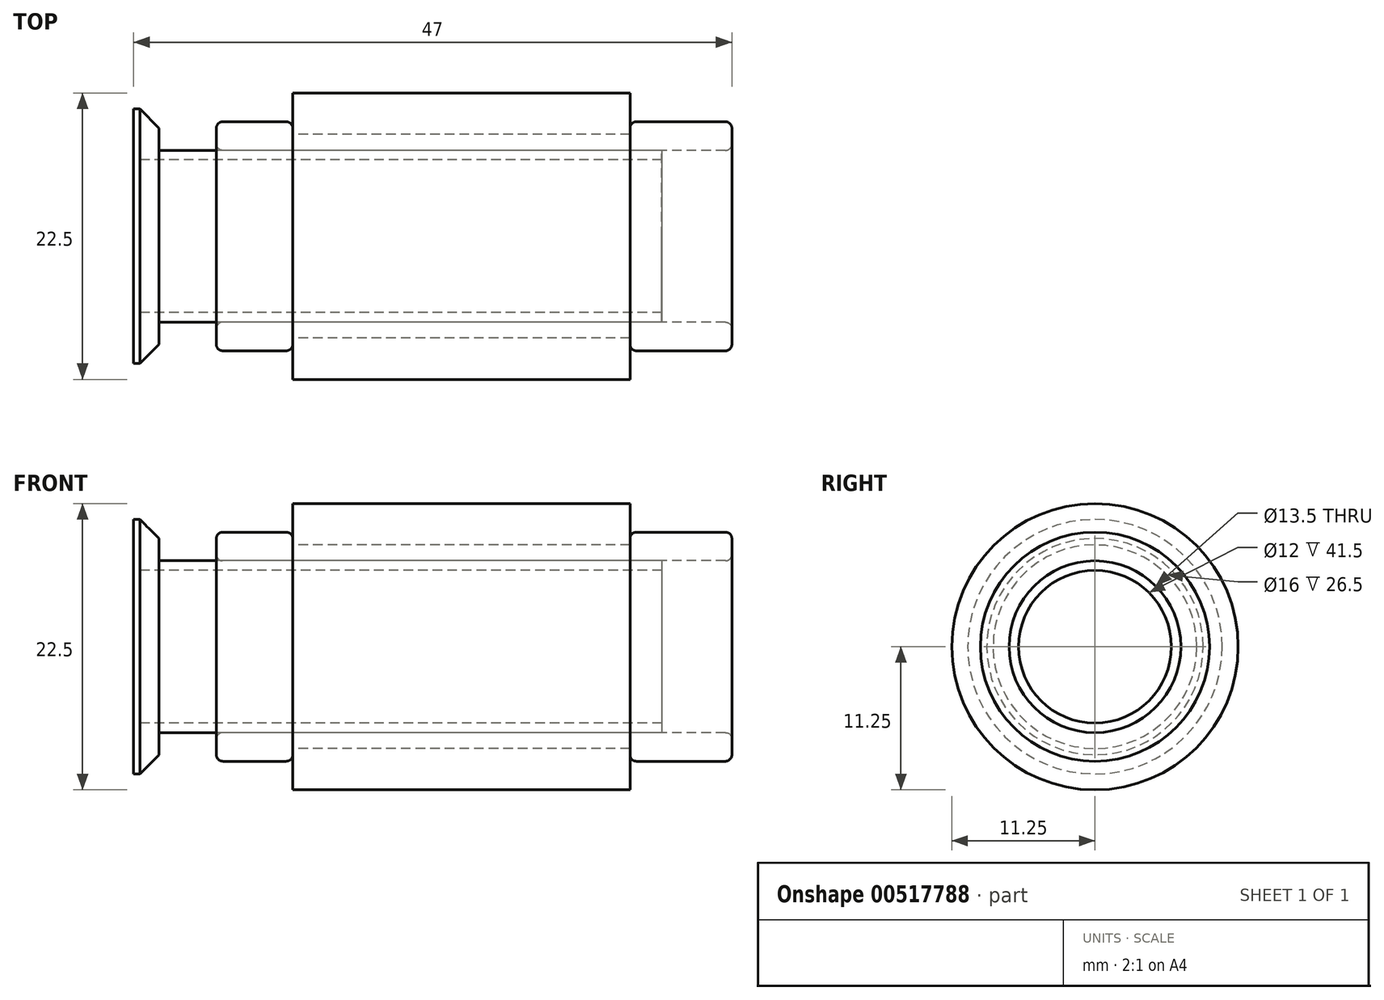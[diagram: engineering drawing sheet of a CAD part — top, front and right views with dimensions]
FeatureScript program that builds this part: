
annotation { "Feature Type Name" : "Feature", "Feature Type Description" : "" }
export const myFeature = defineFeature(function(context is Context, id is Id, definition is map)
    precondition{}
    {
        {
            var Q0;
            Q0=qCreatedBy(makeId("Front.planeOp"),FACE);
            var sketch = newSketch(context, id + "F0", { "sketchPlane" : qUnion([Q0])});
            skLineSegment(sketch, "E0.bottom", {"start": v(0, 11.25) * mm, "end": v(26.5, 11.25) * mm});
            skLineSegment(sketch, "E0.top", {"start": v(0, 8) * mm, "end": v(26.5, 8) * mm});
            skLineSegment(sketch, "E0.left", {"start": v(0, 11.25) * mm, "end": v(0, 8) * mm});
            skLineSegment(sketch, "E0.right", {"start": v(26.5, 11.25) * mm, "end": v(26.5, 8) * mm});
            skLineSegment(sketch, "E1", {"start": v(-6.13, 0) * mm, "end": v(35.82, 0) * mm});
            skSolve(sketch);
        }
        {
            var Q0;
            Q0 = qSketchRegion(id + "F0", true);
            var Q1;
            Q1=sQuery(id+"F0.wireOp",EDGE,"E1");
            revolve(context, id + "F1", {"entities" : qUnion([Q0]), "axis" : qUnion([Q1]), "revolveType" : RevolveType.FULL});
        }
        {
            var Q0;
            Q0=qCreatedBy(makeId("Front.planeOp"),FACE);
            var sketch = newSketch(context, id + "F2", { "sketchPlane" : qUnion([Q0])});
            skLineSegment(sketch, "E2", {"start": v(-10.5, 6.75) * mm, "end": v(29, 6.75) * mm});
            skLineSegment(sketch, "E3", {"start": v(29, 6.75) * mm, "end": v(29, 6) * mm});
            skLineSegment(sketch, "E4", {"start": v(29, 6) * mm, "end": v(-12.5, 6) * mm});
            skLineSegment(sketch, "E5", {"start": v(-12.5, 6) * mm, "end": v(-12.5, 10) * mm});
            skLineSegment(sketch, "E6", {"start": v(-12.5, 10) * mm, "end": v(-12, 10) * mm});
            skLineSegment(sketch, "E7", {"start": v(-12, 10) * mm, "end": v(-10.5, 8.5) * mm});
            skLineSegment(sketch, "E8", {"start": v(-10.5, 8.5) * mm, "end": v(-10.5, 6.75) * mm});
            skLineSegment(sketch, "E9", {"start": v(-7.68, 0) * mm, "end": v(-2.98, 0) * mm});
            skSolve(sketch);
        }
        {
            var Q0;
            Q0=makeQuery(id+"F2.imprint","IMPRINT",FACE,{"disambiguationData":[TD([[makeQuery(id+"F2.imprint","IMPRINT",EDGE,{"derivedFrom":sQuery(id+"F2.wireOp",EDGE,"E2")}),-1.0]])]});
            var Q1;
            Q1=sQuery(id+"F2.wireOp",EDGE,"E9");
            revolve(context, id + "F3", {"entities" : qUnion([Q0]), "axis" : qUnion([Q1]), "revolveType" : RevolveType.FULL});
        }
        {
            var Q0;
            Q0=qCreatedBy(makeId("Front.planeOp"),FACE);
            var sketch = newSketch(context, id + "F4", { "sketchPlane" : qUnion([Q0])});
            skLineSegment(sketch, "E10.bottom", {"start": v(-5.5, 9) * mm, "end": v(-0.5, 9) * mm});
            skLineSegment(sketch, "E10.left", {"start": v(-6, 8.5) * mm, "end": v(-6, 7.25) * mm});
            skLineSegment(sketch, "E10.right", {"start": v(0, 8.5) * mm, "end": v(0, 8) * mm});
            skLineSegment(sketch, "E11.bottom", {"start": v(27, 9) * mm, "end": v(34, 9) * mm});
            skLineSegment(sketch, "E11.top", {"start": v(26.5, 6.75) * mm, "end": v(34, 6.75) * mm});
            skLineSegment(sketch, "E11.left", {"start": v(26.5, 8.5) * mm, "end": v(26.5, 8) * mm});
            skLineSegment(sketch, "E11.right", {"start": v(34.5, 8.5) * mm, "end": v(34.5, 7.25) * mm});
            skLineSegment(sketch, "E12.bottom", {"start": v(0, 8) * mm, "end": v(26.5, 8) * mm});
            skLineSegment(sketch, "E12.top", {"start": v(-5.5, 6.75) * mm, "end": v(26.5, 6.75) * mm});
            skPoint(sketch, "E13.visualSharp", {"position": v(-6, 9) * mm});
            skArc(sketch, "E13.filletArc", {"start": v(-5.5, 9) * mm, "mid": v(-5.85, 8.85) * mm, "end": v(-6, 8.5) * mm});
            skPoint(sketch, "E14.visualSharp", {"position": v(-6, 6.75) * mm});
            skArc(sketch, "E14.filletArc", {"start": v(-6, 7.25) * mm, "mid": v(-5.85, 6.9) * mm, "end": v(-5.5, 6.75) * mm});
            skPoint(sketch, "E15.visualSharp", {"position": v(0, 9) * mm});
            skArc(sketch, "E15.filletArc", {"start": v(0, 8.5) * mm, "mid": v(-0.15, 8.85) * mm, "end": v(-0.5, 9) * mm});
            skPoint(sketch, "E16.visualSharp", {"position": v(26.5, 9) * mm});
            skArc(sketch, "E16.filletArc", {"start": v(27, 9) * mm, "mid": v(26.65, 8.85) * mm, "end": v(26.5, 8.5) * mm});
            skPoint(sketch, "E17.visualSharp", {"position": v(34.5, 9) * mm});
            skArc(sketch, "E17.filletArc", {"start": v(34.5, 8.5) * mm, "mid": v(34.35, 8.85) * mm, "end": v(34, 9) * mm});
            skPoint(sketch, "E18.visualSharp", {"position": v(34.5, 6.75) * mm});
            skArc(sketch, "E18.filletArc", {"start": v(34, 6.75) * mm, "mid": v(34.35, 6.9) * mm, "end": v(34.5, 7.25) * mm});
            skLineSegment(sketch, "E19", {"start": v(-24.6, 0) * mm, "end": v(-19.31, 0) * mm});
            skSolve(sketch);
        }
        {
            var Q0;
            Q0=makeQuery(id+"F4.imprint","IMPRINT",FACE,{"disambiguationData":[TD([[makeQuery(id+"F4.imprint","IMPRINT",EDGE,{"derivedFrom":sQuery(id+"F4.wireOp",EDGE,"E10.bottom")}),-1.0]])]});
            var Q1;
            Q1 = qConstructionFilter(qBodyType(qCreatedBy(id + "F4" ,EDGE), BodyType.WIRE), ConstructionObject.NO);
            var Q2;
            Q2=sQuery(id+"F4.wireOp",EDGE,"E19");
            revolve(context, id + "F5", {"entities" : qUnion([Q0]), "surfaceEntities" : qUnion([Q1]), "axis" : qUnion([Q2]), "revolveType" : RevolveType.FULL});
        }
    });
